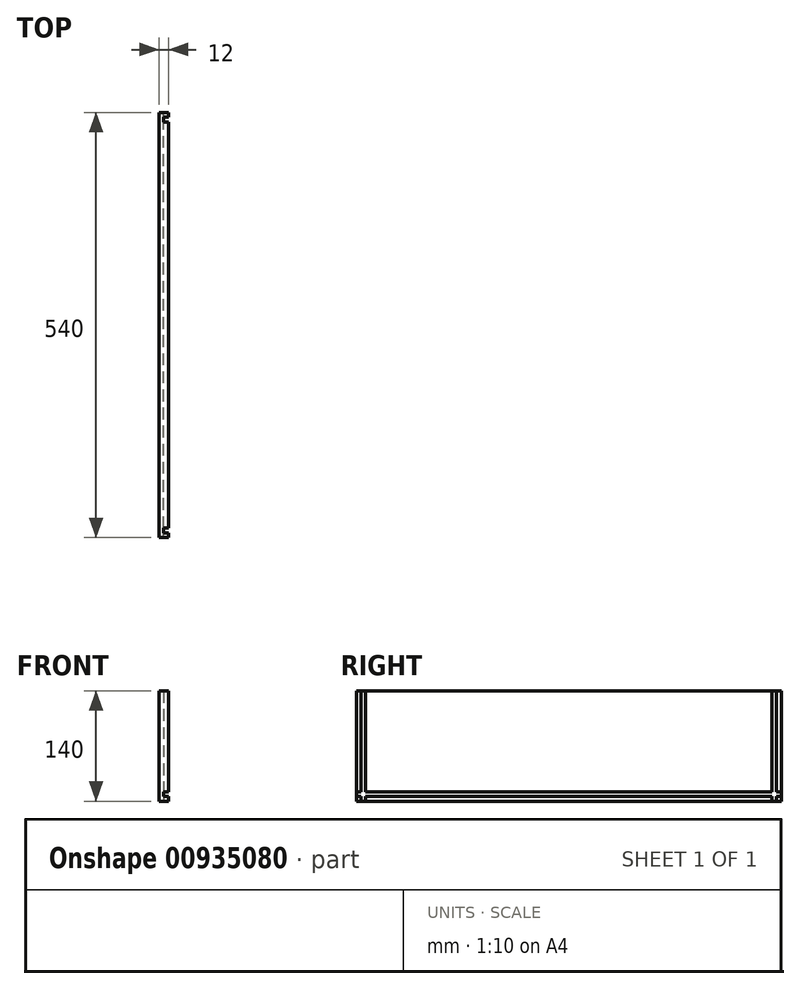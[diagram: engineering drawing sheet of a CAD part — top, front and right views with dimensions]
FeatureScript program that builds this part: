
annotation { "Feature Type Name" : "Feature", "Feature Type Description" : "" }
export const myFeature = defineFeature(function(context is Context, id is Id, definition is map)
    precondition{}
    {
        {
            var Q0;
            Q0=qCreatedBy(makeId("Front.planeOp"),FACE);
            var sketch = newSketch(context, id + "F0", { "sketchPlane" : qUnion([Q0])});
            skLineSegment(sketch, "E0.bottom", {"start": v(0, 0) * mm, "end": v(12, 0) * mm});
            skLineSegment(sketch, "E0.top", {"start": v(0, 140) * mm, "end": v(12, 140) * mm});
            skLineSegment(sketch, "E0.left", {"start": v(0, 0) * mm, "end": v(0, 140) * mm});
            skLineSegment(sketch, "E0.right", {"start": v(12, 0) * mm, "end": v(12, 140) * mm});
            skSolve(sketch);
        }
        {
            var Q0;
            Q0=makeQuery(id+"F0.imprint","IMPRINT",FACE,{"disambiguationData":[TD([[makeQuery(id+"F0.imprint","IMPRINT",EDGE,{"derivedFrom":sQuery(id+"F0.wireOp",EDGE,"E0.bottom")}),1.0]])]});
            extrude(context, id + "F1", {"entities" : qUnion([Q0]), "depth" : 540 * mm, "offsetDistance" : 25 * mm});
        }
        {
            var Q0;
            Q0=qCreatedBy(makeId("Top.planeOp"),FACE);
            var sketch = newSketch(context, id + "F2", { "sketchPlane" : qUnion([Q0])});
            skLineSegment(sketch, "E1.0", {"start": v(12, -540) * mm, "end": v(12, 0) * mm, "construction": true});
            skLineSegment(sketch, "E2.bottom", {"start": v(12, -6) * mm, "end": v(6, -6) * mm});
            skLineSegment(sketch, "E2.top", {"start": v(12, -12) * mm, "end": v(6, -12) * mm});
            skLineSegment(sketch, "E2.left", {"start": v(12, -6) * mm, "end": v(12, -12) * mm});
            skLineSegment(sketch, "E2.right", {"start": v(6, -6) * mm, "end": v(6, -12) * mm});
            skLineSegment(sketch, "E3.bottom", {"start": v(12, -534) * mm, "end": v(6, -534) * mm});
            skLineSegment(sketch, "E3.top", {"start": v(12, -528) * mm, "end": v(6, -528) * mm});
            skLineSegment(sketch, "E3.left", {"start": v(12, -534) * mm, "end": v(12, -528) * mm});
            skLineSegment(sketch, "E3.right", {"start": v(6, -534) * mm, "end": v(6, -528) * mm});
            skSolve(sketch);
        }
        {
            var Q0;
            Q0=qSketchRegion(id+"F2",true);
            extrude(context, id + "F3", {"entities" : qUnion([Q0]), "operationType" : NewBodyOperationType.REMOVE, "endBound" : BoundingType.THROUGH_ALL, "depth" : 25 * mm, "offsetDistance" : 25 * mm});
        }
        {
            var Q0;
            Q0=makeQuery(id+"F1.opExtrude","CAP_FACE",FACE,{"disambiguationData":[OSD([sQuery(id+"F0.wireOp",EDGE,"E0.bottom"),sQuery(id+"F0.wireOp",EDGE,"E0.top"),sQuery(id+"F0.wireOp",EDGE,"E0.left"),sQuery(id+"F0.wireOp",EDGE,"E0.right")])],"isStart":true});
            var sketch = newSketch(context, id + "F4", { "sketchPlane" : qUnion([Q0])});
            skLineSegment(sketch, "E4.bottom", {"start": v(-6, 6) * mm, "end": v(-12, 6) * mm});
            skLineSegment(sketch, "E4.top", {"start": v(-6, 12) * mm, "end": v(-12, 12) * mm});
            skLineSegment(sketch, "E4.left", {"start": v(-6, 6) * mm, "end": v(-6, 12) * mm});
            skLineSegment(sketch, "E4.right", {"start": v(-12, 6) * mm, "end": v(-12, 12) * mm});
            skSolve(sketch);
        }
        {
            var Q0;
            Q0=qSketchRegion(id+"F4",true);
            var Q1;
            Q1=makeQuery(id+"F3.boolean.opBoolean","COPY",FACE,{"derivedFrom":makeQuery(id+"F3.opExtrude","SWEPT_FACE",FACE,{"disambiguationData":[OSD([sQuery(id+"F2.wireOp",EDGE,"E3.top")])]})});
            extrude(context, id + "F5", {"entities" : qUnion([Q0]), "operationType" : NewBodyOperationType.REMOVE, "endBound" : BoundingType.THROUGH_ALL, "oppositeDirection" : true, "depth" : 25 * mm, "endBoundEntityFace" : qUnion([Q1]), "offsetDistance" : 25 * mm});
        }
    });
